FCSTD DOCUMENT  (FreeCAD 0.21R33668 +26 (Git))
Label: RotateEngine-003
License: All rights reserved
LicenseURL: http://en.wikipedia.org/wiki/All_rights_reserved
objects: App::DocumentObjectGroup×3, PartDesign::CoordinateSystem×2, Sketcher::SketchObject×2, App::FeaturePython×1, App::Part×1
note: 4 computed .brp shape members not serialized (recipe doc carries the construction recipe); baked Part::Feature solids carry a one-line shape summary decoded from their .brp

FEATURE [App::DocumentObjectGroup] Parts
FEATURE [App::DocumentObjectGroup] Constraints
FEATURE [App::FeaturePython] Variables  # WARN: FeaturePython — macro-defined, semantics opaque (R4)
  Angle_Rotation = 636
  Longueur_1 = 558
  Type = App::PropertyContainer
FEATURE [App::DocumentObjectGroup] Configurations
FEATURE [PartDesign::CoordinateSystem] LCS_Mobile  label="LCS_Engine"
  AttacherType = Attacher::AttachEngine3D
  AttachmentOffset = pos=(200,0,-370) rot=(0,0,1;0rad)
  MapMode = 2
  Placement = pos=(200,0,-370) rot=(0,0,1;0rad)
  Support = -> [X_Axis]
FEATURE [Sketcher::SketchObject] Barre  label="Sketch_Engine"
  AttachmentOffset = pos=(0,0,0) rot=(0,0,1;11.1003rad)
  FullyConstrained = false
  MapMode = 3
  Placement = pos=(200,0,-370) rot=(-0.617631,-0.556117,0.556117;4.24816rad)
  Support = -> [LCS_Mobile]
  expr: .AttachmentOffset.Rotation.Angle = Variables.Angle_Rotation
  sketch-geometry (2):
    g0: Circle CenterX=0 CenterY=0 CenterZ=0 NormalX=0 NormalY=0 NormalZ=1 AngleXU=0 Radius=105
    g1: LineSegment StartX=0 StartY=0 StartZ=0 EndX=-102.617 EndY=22.2437 EndZ=0
  constraints (4):
    c: Coincident(g0,g-1)
    c: Radius(g0) = 105
    c: Coincident(g1,g0)
    c: PointOnObject(g1,g0)
FEATURE [PartDesign::CoordinateSystem] LCS_Origin
  AttacherType = Attacher::AttachEngine3D
  MapMode = 2
  Support = -> [X_Axis]
FEATURE [Sketcher::SketchObject] Sketch_Leg  label="Sketch_Finger"
  ExternalGeometry = -> [Barre]
  FullyConstrained = true
  MapMode = 3
  Placement = pos=(0,0,0) rot=(1,0,0;1.5708rad)
  Support = -> [LCS_Origin]
  expr: Constraints[0] = Variables.Longueur_1 * 1
  expr: Constraints[1] = Variables.Longueur_1 * 0.619
  expr: Constraints[2] = Variables.Longueur_1 * 0.7437
  expr: Constraints[3] = Variables.Longueur_1 * 0.711
  expr: Constraints[4] = Variables.Longueur_1 * 0.704
  expr: Constraints[5] = Variables.Longueur_1 * 0.8976
  expr: Constraints[6] = Variables.Longueur_1 * 1.094
  expr: Constraints[7] = Variables.Longueur_1 * 1.1774
  expr: Constraints[8] = Variables.Longueur_1 * 0.878
  expr: Constraints[9] = Variables.Longueur_1 * 0.6
  sketch-geometry (10):
    g0: LineSegment StartX=0 StartY=0 StartZ=0 EndX=-288.392 EndY=-298.4 EndZ=0
    g1: LineSegment StartX=-288.392 StartY=-298.4 StartZ=0 EndX=-231.15 EndY=256.656 EndZ=0
    g2: LineSegment StartX=0 StartY=0 StartZ=0 EndX=-231.15 EndY=256.656 EndZ=0
    g3: LineSegment StartX=-288.392 StartY=-298.4 StartZ=0 EndX=211.395 EndY=-265.62 EndZ=0
    g4: LineSegment StartX=211.395 StartY=-265.62 StartZ=0 EndX=196.513 EndY=344.65 EndZ=0
    g5: LineSegment StartX=-231.15 StartY=256.656 StartZ=0 EndX=-28.089 EndY=592.935 EndZ=0
    g6: LineSegment StartX=196.513 StartY=344.65 StartZ=0 EndX=-28.089 EndY=592.935 EndZ=0
    g7: LineSegment StartX=196.513 StartY=344.65 StartZ=0 EndX=0 EndY=0 EndZ=0
    g8: LineSegment StartX=-28.089 StartY=592.935 StartZ=0 EndX=628.667 EndY=575.448 EndZ=0
    g9: LineSegment StartX=628.667 StartY=575.448 StartZ=0 EndX=196.513 EndY=344.65 EndZ=0
  constraints (25):
    c: Distance(g1) = 558
    c: Distance(g2) = 345.402
    c: Distance(g0) = 414.985
    c: Distance(g7) = 396.738
    c: Distance(g5) = 392.832
    c: Distance(g3) = 500.861
    c: Distance(g4) = 610.452
    c: Distance(g8) = 656.989
    c: Distance(g9) = 489.924
    c: Distance(g6) = 334.8
    c: Coincident(g8,g9)
    c: Coincident(g8,g6)
    c: Coincident(g8,g5)
    c: Coincident(g7,g6)
    c: Coincident(g7,g9)
    c: Coincident(g7,g4)
    c: Coincident(g0,g-1)
    c: Coincident(g0,g2)
    c: Coincident(g0,g7)
    c: Coincident(g4,g3)
    c: Coincident(g1,g5)
    c: Coincident(g1,g2)
    c: Coincident(g0,g3)
    c: Coincident(g0,g1)
    c: Coincident(g-3,g3)
FEATURE [App::Part] Assembly
  AssemblyType = Part::Link
  Group = -> [Constraints,Variables,Configurations,Barre,LCS_Mobile,Sketch_Leg,LCS_Origin]
  Origin = -> Origin
  Type = Assembly
